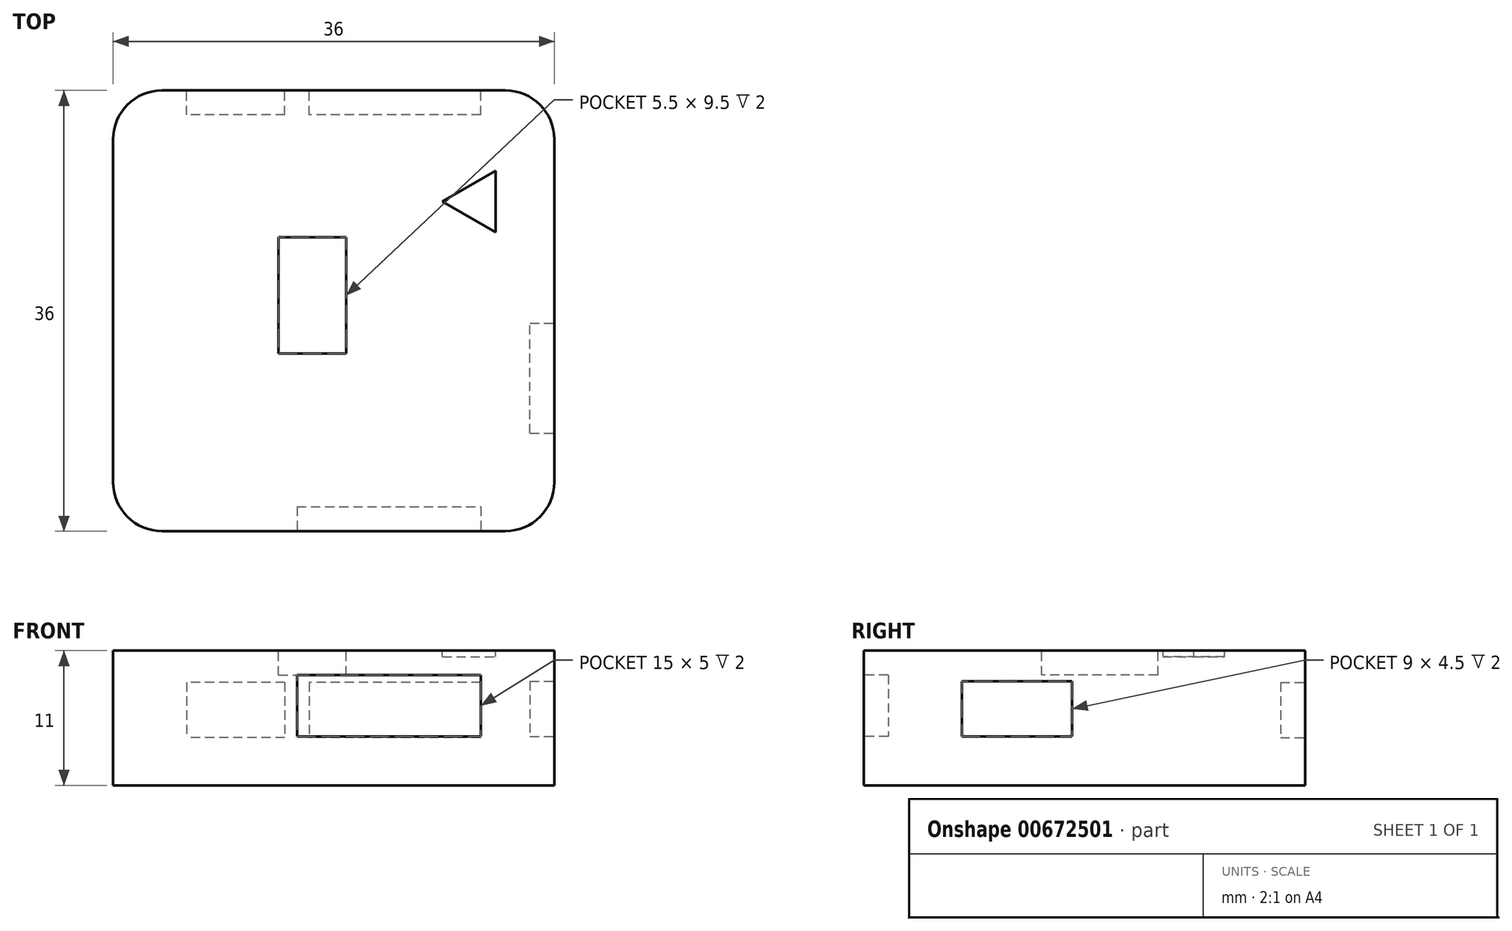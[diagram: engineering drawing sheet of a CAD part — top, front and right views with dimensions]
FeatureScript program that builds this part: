
annotation { "Feature Type Name" : "Feature", "Feature Type Description" : "" }
export const myFeature = defineFeature(function(context is Context, id is Id, definition is map)
    precondition{}
    {
        {
            var Q0;
            Q0=qCreatedBy(makeId("Top.planeOp"),FACE);
            var sketch = newSketch(context, id + "F0", { "sketchPlane" : qUnion([Q0])});
            skLineSegment(sketch, "E0.bottom", {"start": v(-14, 18) * mm, "end": v(14, 18) * mm});
            skLineSegment(sketch, "E0.top", {"start": v(-14, -18) * mm, "end": v(14, -18) * mm});
            skLineSegment(sketch, "E0.left", {"start": v(-18, 14) * mm, "end": v(-18, -14) * mm});
            skLineSegment(sketch, "E0.right", {"start": v(18, 14) * mm, "end": v(18, -14) * mm});
            skPoint(sketch, "E1.visualSharp", {"position": v(-18, 18) * mm});
            skArc(sketch, "E1.filletArc", {"start": v(-14, 18) * mm, "mid": v(-16.83, 16.83) * mm, "end": v(-18, 14) * mm});
            skPoint(sketch, "E2.visualSharp", {"position": v(18, 18) * mm});
            skArc(sketch, "E2.filletArc", {"start": v(18, 14) * mm, "mid": v(16.83, 16.83) * mm, "end": v(14, 18) * mm});
            skPoint(sketch, "E3.visualSharp", {"position": v(18, -18) * mm});
            skArc(sketch, "E3.filletArc", {"start": v(14, -18) * mm, "mid": v(16.83, -16.83) * mm, "end": v(18, -14) * mm});
            skPoint(sketch, "E4.visualSharp", {"position": v(-18, -18) * mm});
            skArc(sketch, "E4.filletArc", {"start": v(-18, -14) * mm, "mid": v(-16.83, -16.83) * mm, "end": v(-14, -18) * mm});
            skSolve(sketch);
        }
        {
            var Q0;
            Q0=makeQuery(id+"F0.imprint","IMPRINT",FACE,{"disambiguationData":[TD([[makeQuery(id+"F0.imprint","IMPRINT",EDGE,{"derivedFrom":sQuery(id+"F0.wireOp",EDGE,"E0.bottom")}),-1.0]])]});
            extrude(context, id + "F1", {"entities" : qUnion([Q0]), "depth" : 11 * mm, "offsetDistance" : 25 * mm});
        }
        {
            var Q0;
            Q0=makeQuery(id+"F1.opExtrude","SWEPT_FACE",FACE,{"disambiguationData":[OSD([sQuery(id+"F0.wireOp",EDGE,"E0.top")])]});
            var sketch = newSketch(context, id + "F2", { "sketchPlane" : qUnion([Q0])});
            skLineSegment(sketch, "E5.bottom", {"start": v(-3, 9) * mm, "end": v(12, 9) * mm});
            skLineSegment(sketch, "E5.top", {"start": v(-3, 4) * mm, "end": v(12, 4) * mm});
            skLineSegment(sketch, "E5.left", {"start": v(-3, 9) * mm, "end": v(-3, 4) * mm});
            skLineSegment(sketch, "E5.right", {"start": v(12, 9) * mm, "end": v(12, 4) * mm});
            skSolve(sketch);
        }
        {
            var Q0;
            Q0 = qSketchRegion(id + "F2", true);
            extrude(context, id + "F3", {"entities" : qUnion([Q0]), "operationType" : NewBodyOperationType.REMOVE, "oppositeDirection" : true, "depth" : 2 * mm, "offsetDistance" : 25 * mm});
        }
        {
            var Q0;
            Q0=makeQuery(id+"F1.opExtrude","SWEPT_FACE",FACE,{"disambiguationData":[OSD([sQuery(id+"F0.wireOp",EDGE,"E0.right")])]});
            var sketch = newSketch(context, id + "F4", { "sketchPlane" : qUnion([Q0])});
            skLineSegment(sketch, "E6.bottom", {"start": v(-10, 8.5) * mm, "end": v(-1, 8.5) * mm});
            skLineSegment(sketch, "E6.top", {"start": v(-10, 4) * mm, "end": v(-1, 4) * mm});
            skLineSegment(sketch, "E6.left", {"start": v(-10, 8.5) * mm, "end": v(-10, 4) * mm});
            skLineSegment(sketch, "E6.right", {"start": v(-1, 8.5) * mm, "end": v(-1, 4) * mm});
            skSolve(sketch);
        }
        {
            var Q0;
            Q0=makeQuery(id+"F4.imprint","IMPRINT",FACE,{"disambiguationData":[TD([[makeQuery(id+"F4.imprint","IMPRINT",EDGE,{"derivedFrom":sQuery(id+"F4.wireOp",EDGE,"E6.bottom")}),-1.0]])]});
            extrude(context, id + "F5", {"entities" : qUnion([Q0]), "operationType" : NewBodyOperationType.REMOVE, "oppositeDirection" : true, "depth" : 2 * mm, "offsetDistance" : 25 * mm});
        }
        {
            var Q0;
            Q0=makeQuery(id+"F1.opExtrude","SWEPT_FACE",FACE,{"disambiguationData":[OSD([sQuery(id+"F0.wireOp",EDGE,"E0.bottom")])]});
            var sketch = newSketch(context, id + "F6", { "sketchPlane" : qUnion([Q0])});
            skLineSegment(sketch, "E7.bottom", {"start": v(-12, 8.4) * mm, "end": v(2, 8.4) * mm});
            skLineSegment(sketch, "E7.top", {"start": v(-12, 3.9) * mm, "end": v(2, 3.9) * mm});
            skLineSegment(sketch, "E7.left", {"start": v(-12, 8.4) * mm, "end": v(-12, 3.9) * mm});
            skLineSegment(sketch, "E7.right", {"start": v(2, 8.4) * mm, "end": v(2, 3.9) * mm});
            skLineSegment(sketch, "E8.bottom", {"start": v(4, 8.4) * mm, "end": v(12, 8.4) * mm});
            skLineSegment(sketch, "E8.top", {"start": v(4, 3.9) * mm, "end": v(12, 3.9) * mm});
            skLineSegment(sketch, "E8.left", {"start": v(4, 8.4) * mm, "end": v(4, 3.9) * mm});
            skLineSegment(sketch, "E8.right", {"start": v(12, 8.4) * mm, "end": v(12, 3.9) * mm});
            skSolve(sketch);
        }
        {
            var Q0;
            Q0=makeQuery(id+"F6.imprint","IMPRINT",FACE,{"disambiguationData":[TD([[makeQuery(id+"F6.imprint","IMPRINT",EDGE,{"derivedFrom":sQuery(id+"F6.wireOp",EDGE,"E7.bottom")}),-1.0]])]});
            var Q1;
            Q1=makeQuery(id+"F6.imprint","IMPRINT",FACE,{"disambiguationData":[TD([[makeQuery(id+"F6.imprint","IMPRINT",EDGE,{"derivedFrom":sQuery(id+"F6.wireOp",EDGE,"E8.bottom")}),-1.0]])]});
            extrude(context, id + "F7", {"entities" : qUnion([Q0, Q1]), "operationType" : NewBodyOperationType.REMOVE, "oppositeDirection" : true, "depth" : 2 * mm, "offsetDistance" : 25 * mm});
        }
        {
            var Q0;
            Q0=makeQuery(id+"F1.opExtrude","CAP_FACE",FACE,{"disambiguationData":[OSD([sQuery(id+"F0.wireOp",EDGE,"E0.bottom"),sQuery(id+"F0.wireOp",EDGE,"E0.top"),sQuery(id+"F0.wireOp",EDGE,"E0.left"),sQuery(id+"F0.wireOp",EDGE,"E0.right"),sQuery(id+"F0.wireOp",EDGE,"E1.filletArc"),sQuery(id+"F0.wireOp",EDGE,"E2.filletArc"),sQuery(id+"F0.wireOp",EDGE,"E3.filletArc"),sQuery(id+"F0.wireOp",EDGE,"E4.filletArc")])],"isStart":false});
            var sketch = newSketch(context, id + "F8", { "sketchPlane" : qUnion([Q0])});
            skLineSegment(sketch, "E9.bottom", {"start": v(-4.5, 6) * mm, "end": v(1, 6) * mm});
            skLineSegment(sketch, "E9.left", {"start": v(1, 6) * mm, "end": v(1, -3.5) * mm});
            skLineSegment(sketch, "E10", {"start": v(8.87, 8.93) * mm, "end": v(13.2, 11.43) * mm});
            skLineSegment(sketch, "E11", {"start": v(13.2, 11.43) * mm, "end": v(13.2, 6.43) * mm});
            skLineSegment(sketch, "E12", {"start": v(13.2, 6.43) * mm, "end": v(8.87, 8.93) * mm});
            skLineSegment(sketch, "E13", {"start": v(-4.5, 6) * mm, "end": v(-4.5, -3.5) * mm});
            skLineSegment(sketch, "E14", {"start": v(-4.5, -3.5) * mm, "end": v(1, -3.5) * mm});
            skSolve(sketch);
        }
        {
            var Q0;
            Q0=makeQuery(id+"F8.imprint","IMPRINT",FACE,{"disambiguationData":[TD([[makeQuery(id+"F8.imprint","IMPRINT",EDGE,{"derivedFrom":sQuery(id+"F8.wireOp",EDGE,"E9.bottom")}),-1.0]])]});
            extrude(context, id + "F9", {"entities" : qUnion([Q0]), "operationType" : NewBodyOperationType.REMOVE, "oppositeDirection" : true, "depth" : 2 * mm, "offsetDistance" : 25 * mm});
        }
        {
            var Q0;
            Q0=makeQuery(id+"F8.imprint","IMPRINT",FACE,{"disambiguationData":[TD([[makeQuery(id+"F8.imprint","IMPRINT",EDGE,{"derivedFrom":sQuery(id+"F8.wireOp",EDGE,"E10")}),-1.0]])]});
            extrude(context, id + "F10", {"entities" : qUnion([Q0]), "operationType" : NewBodyOperationType.REMOVE, "oppositeDirection" : true, "depth" : 0.5 * mm, "offsetDistance" : 25 * mm});
        }
    });
